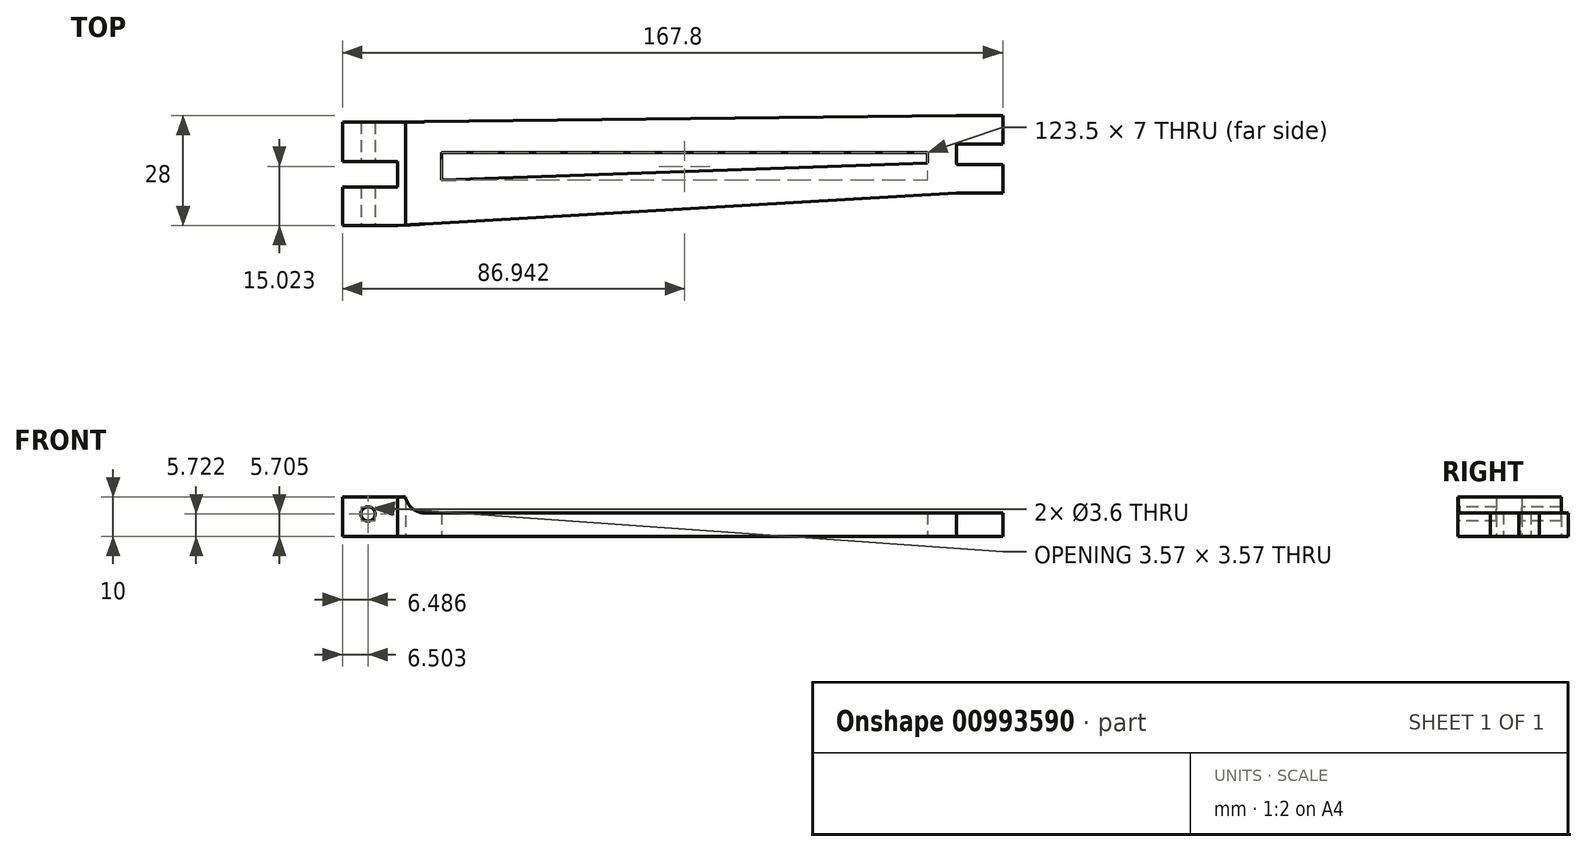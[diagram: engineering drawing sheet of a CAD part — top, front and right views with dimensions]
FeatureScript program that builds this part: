
annotation { "Feature Type Name" : "Feature", "Feature Type Description" : "" }
export const myFeature = defineFeature(function(context is Context, id is Id, definition is map)
    precondition{}
    {
        {
            var Q0;
            Q0=qCreatedBy(makeId("Top.planeOp"),FACE);
            var sketch = newSketch(context, id + "F0", { "sketchPlane" : qUnion([Q0])});
            skLineSegment(sketch, "E0.bottom", {"start": v(46.15, 35.49) * mm, "end": v(51.95, 35.49) * mm});
            skLineSegment(sketch, "E0.top", {"start": v(46.15, 28.19) * mm, "end": v(51.95, 28.19) * mm});
            skLineSegment(sketch, "E0.left", {"start": v(46.15, 35.49) * mm, "end": v(46.15, 28.19) * mm});
            skLineSegment(sketch, "E0.right", {"start": v(51.95, 35.49) * mm, "end": v(51.95, 28.19) * mm});
            skLineSegment(sketch, "E1.bottom", {"start": v(46.15, 22.99) * mm, "end": v(51.95, 22.99) * mm});
            skLineSegment(sketch, "E1.top", {"start": v(46.15, 15.69) * mm, "end": v(51.95, 15.69) * mm});
            skLineSegment(sketch, "E1.left", {"start": v(46.15, 22.99) * mm, "end": v(46.15, 15.69) * mm});
            skLineSegment(sketch, "E1.right", {"start": v(51.95, 22.99) * mm, "end": v(51.95, 15.69) * mm});
            skLineSegment(sketch, "E2.bottom", {"start": v(46.15, 35.49) * mm, "end": v(40.15, 35.49) * mm});
            skLineSegment(sketch, "E2.top", {"start": v(46.15, 28.19) * mm, "end": v(40.15, 28.19) * mm});
            skLineSegment(sketch, "E2.right", {"start": v(40.15, 35.49) * mm, "end": v(40.15, 28.19) * mm});
            skLineSegment(sketch, "E3.bottom", {"start": v(46.15, 22.99) * mm, "end": v(46.15, 22.99) * mm});
            skLineSegment(sketch, "E3.top", {"start": v(46.15, 15.69) * mm, "end": v(46.15, 15.69) * mm});
            skLineSegment(sketch, "E4.bottom", {"start": v(40.15, 22.99) * mm, "end": v(46.15, 22.99) * mm});
            skLineSegment(sketch, "E4.top", {"start": v(40.15, 15.69) * mm, "end": v(46.15, 15.69) * mm});
            skLineSegment(sketch, "E4.left", {"start": v(40.15, 22.99) * mm, "end": v(40.15, 15.69) * mm});
            skLineSegment(sketch, "E5.bottom", {"start": v(40.15, 35.49) * mm, "end": v(-99.85, 33.79) * mm});
            skLineSegment(sketch, "E5.left", {"start": v(40.15, 35.49) * mm, "end": v(40.15, 15.69) * mm});
            skLineSegment(sketch, "E6.bottom", {"start": v(-90.66, 26.01) * mm, "end": v(32.84, 26.01) * mm});
            skLineSegment(sketch, "E6.left", {"start": v(-90.66, 26.01) * mm, "end": v(-90.66, 19.02) * mm});
            skLineSegment(sketch, "E6.right", {"start": v(32.84, 26.01) * mm, "end": v(32.84, 23.4) * mm});
            skLineSegment(sketch, "E7", {"start": v(-101.85, 7.49) * mm, "end": v(40.15, 15.69) * mm});
            skLineSegment(sketch, "E8.left", {"start": v(-90.66, 19.02) * mm, "end": v(-90.66, 19.02) * mm});
            skLineSegment(sketch, "E9", {"start": v(-90.66, 19.02) * mm, "end": v(32.84, 23.4) * mm});
            skLineSegment(sketch, "E10.bottom", {"start": v(-99.85, 33.79) * mm, "end": v(-115.85, 33.79) * mm});
            skLineSegment(sketch, "E11.bottom", {"start": v(-115.85, 23.79) * mm, "end": v(-101.85, 23.79) * mm});
            skLineSegment(sketch, "E11.right", {"start": v(-101.85, 23.79) * mm, "end": v(-101.85, 17.29) * mm});
            skLineSegment(sketch, "E12", {"start": v(-115.85, 33.79) * mm, "end": v(-115.85, 23.79) * mm});
            skLineSegment(sketch, "E13.bottom", {"start": v(-101.85, 17.29) * mm, "end": v(-115.85, 17.29) * mm});
            skLineSegment(sketch, "E13.top", {"start": v(-101.85, 7.49) * mm, "end": v(-115.85, 7.49) * mm});
            skLineSegment(sketch, "E13.left", {"start": v(-101.85, 17.29) * mm, "end": v(-101.85, 7.49) * mm});
            skLineSegment(sketch, "E13.right", {"start": v(-115.85, 17.29) * mm, "end": v(-115.85, 7.49) * mm});
            skLineSegment(sketch, "E14.bottom", {"start": v(-101.85, 23.79) * mm, "end": v(-115.85, 23.79) * mm});
            skLineSegment(sketch, "E14.right", {"start": v(-115.85, 23.79) * mm, "end": v(-115.85, 31.29) * mm});
            skLineSegment(sketch, "E15", {"start": v(-99.85, 33.79) * mm, "end": v(-99.85, 7.6) * mm});
            skSolve(sketch);
        }
        {
            var Q0;
            {var subQ2=makeQuery(id+"F0.imprint","IMPRINT",EDGE,{"derivedFrom":sQuery(id+"F0.wireOp",EDGE,"E2.right")});var subQ9=sQuery(id+"F0.wireOp",EDGE,"E10.bottom");var subQ15=makeQuery(id+"F0.imprint","IMPRINT",EDGE,{"derivedFrom":sQuery(id+"F0.wireOp",EDGE,"E1.left")});var subQ16=makeQuery(id+"F0.imprint","IMPRINT",EDGE,{"derivedFrom":sQuery(id+"F0.wireOp",EDGE,"E0.left")});Q0=qUnion([makeQuery(id+"F0.imprint","IMPRINT",FACE,{"disambiguationData":[TD([[makeQuery(id+"F0.imprint","IMPRINT",EDGE,{"derivedFrom":sQuery(id+"F0.wireOp",EDGE,"E0.bottom")}),-1.0]])]}),makeQuery(id+"F0.imprint","IMPRINT",FACE,{"disambiguationData":[TD([[makeQuery(id+"F0.imprint","IMPRINT",EDGE,{"derivedFrom":sQuery(id+"F0.wireOp",EDGE,"E1.bottom")}),-1.0]])]}),makeQuery(id+"F0.imprint","IMPRINT",FACE,{"disambiguationData":[TD([[makeQuery(id+"F0.imprint","IMPRINT",EDGE,{"derivedFrom":sQuery(id+"F0.wireOp",EDGE,"E13.bottom")}),1.0]])]}),makeQuery(id+"F0.imprint","IMPRINT",FACE,{"disambiguationData":[TD([[subQ16,-1.0]])]}),makeQuery(id+"F0.imprint","IMPRINT",FACE,{"disambiguationData":[TD([[subQ15,-1.0]])]}),makeQuery(id+"F0.imprint","IMPRINT",FACE,{"disambiguationData":[TD([[makeQuery(id+"F0.imprint","IMPRINT",EDGE,{"derivedFrom":subQ9}),1.0]])]}),makeQuery(id+"F0.imprint","IMPRINT",FACE,{"disambiguationData":[TD([[subQ2,-1.0]])]})]);}
            extrude(context, id + "F1", {"entities" : qUnion([Q0]), "depth" : 6 * mm, "offsetDistance" : 25 * mm});
        }
        {
            var Q0;
            {var subQ1=sQuery(id+"F0.wireOp",EDGE,"E10.bottom");Q0=makeQuery(id+"F0.imprint","IMPRINT",FACE,{"disambiguationData":[TD([[makeQuery(id+"F0.imprint","IMPRINT",EDGE,{"derivedFrom":subQ1}),1.0]])]});}
            var Q1;
            Q1=makeQuery(id+"F0.imprint","IMPRINT",FACE,{"disambiguationData":[TD([[makeQuery(id+"F0.imprint","IMPRINT",EDGE,{"derivedFrom":sQuery(id+"F0.wireOp",EDGE,"E13.bottom")}),1.0]])]});
            extrude(context, id + "F2", {"entities" : qUnion([Q0, Q1]), "operationType" : NewBodyOperationType.ADD, "depth" : 10 * mm, "offsetDistance" : 25 * mm});
        }
        {
            var Q0;
            Q0=qCreatedBy(makeId("Front.planeOp"),FACE);
            var sketch = newSketch(context, id + "F3", { "sketchPlane" : qUnion([Q0])});
            skCircle(sketch, "E16", {"center": v(-109.35, 5.72) * mm, "radius": 1.8 * mm});
            skSolve(sketch);
        }
        {
            var Q0;
            Q0=makeQuery(id+"F3.imprint","IMPRINT",FACE,{"disambiguationData":[TD([[makeQuery(id+"F3.imprint","IMPRINT",EDGE,{"derivedFrom":sQuery(id+"F3.wireOp",EDGE,"E16")}),1.0]])]});
            extrude(context, id + "F4", {"entities" : qUnion([Q0]), "operationType" : NewBodyOperationType.REMOVE, "oppositeDirection" : true, "depth" : 46 * mm, "offsetDistance" : 25 * mm});
        }
        {
            var Q0;
            Q0=makeQuery(id+"F2.boolean.opBoolean","INTERSECT",EDGE,{"derivedFrom":[makeQuery(id+"F1.opExtrude","CAP_FACE",FACE,{"disambiguationData":[OSD([sQuery(id+"F0.wireOp",EDGE,"E0.bottom"),sQuery(id+"F0.wireOp",EDGE,"E0.top"),sQuery(id+"F0.wireOp",EDGE,"E0.right"),sQuery(id+"F0.wireOp",EDGE,"E1.bottom"),sQuery(id+"F0.wireOp",EDGE,"E1.top"),sQuery(id+"F0.wireOp",EDGE,"E1.right"),sQuery(id+"F0.wireOp",EDGE,"E2.bottom"),sQuery(id+"F0.wireOp",EDGE,"E2.top"),sQuery(id+"F0.wireOp",EDGE,"E4.bottom"),sQuery(id+"F0.wireOp",EDGE,"E4.top"),sQuery(id+"F0.wireOp",EDGE,"E5.bottom"),sQuery(id+"F0.wireOp",EDGE,"E5.left"),sQuery(id+"F0.wireOp",EDGE,"E6.bottom"),sQuery(id+"F0.wireOp",EDGE,"E6.left"),sQuery(id+"F0.wireOp",EDGE,"E6.right"),sQuery(id+"F0.wireOp",EDGE,"E7"),sQuery(id+"F0.wireOp",EDGE,"E9"),sQuery(id+"F0.wireOp",EDGE,"E10.bottom"),sQuery(id+"F0.wireOp",EDGE,"E11.bottom"),sQuery(id+"F0.wireOp",EDGE,"E11.right"),sQuery(id+"F0.wireOp",EDGE,"E12"),sQuery(id+"F0.wireOp",EDGE,"E13.bottom"),sQuery(id+"F0.wireOp",EDGE,"E13.top"),sQuery(id+"F0.wireOp",EDGE,"E13.right")])],"isStart":false}),makeQuery(id+"F2.opExtrude","SWEPT_FACE",FACE,{"disambiguationData":[OSD([sQuery(id+"F0.wireOp",EDGE,"E15")])]})]});
            fillet(context, id + "F5", {"entities" : qUnion([Q0]), "radius" : 5 * mm, "tangentPropagation" : true, "allowEdgeOverflow" : false});
        }
    });
